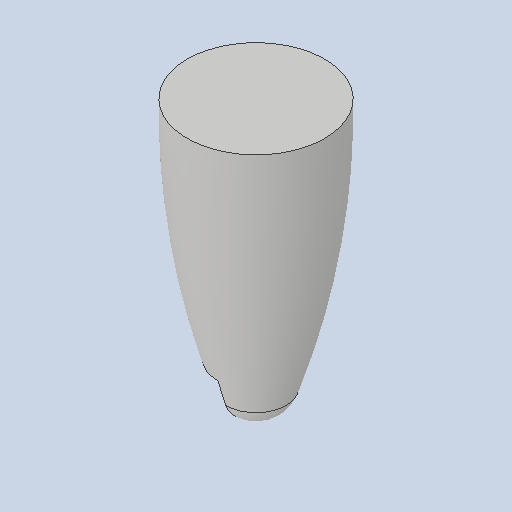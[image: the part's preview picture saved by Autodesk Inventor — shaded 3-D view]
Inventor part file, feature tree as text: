
AUTODESK INVENTOR PART (.ipt)
format: ipt  version: 2024.2 (Build 282272000, 272)  size: 135,680 bytes
history: native  units: mm
features: sketch x3, revolve x2, projected_geometry x2, other x1, extrude x1
ambient origin geometry x8: Origin, YZ Plane, XZ Plane, XY Plane, X Axis, Y Axis, Z Axis, Center Point
bodies: Body1 (feature_tree)
feature tree (9):
  other  "Твердое тело1"
  revolve  "Вращение1"
  revolve  "Вращение2"
  extrude  "Выдавливание1"  Depth=100.0mm
  sketch  "Эскиз1"
  sketch  "Эскиз2"
  projected_geometry  "Спроецированная петля1"
  projected_geometry  "Спроецированная петля2"
  sketch  "Эскиз3"
